# Revit family: Sanitary_Showers_hansgrohe_15854XXX-RainPad-Finish-set-for-2-functi_222
name_source: partatom
category: Plumbing Fixtures
revit_build: Autodesk Revit 2015 (Build: 20140903_1530(x64)
units: mm (PartAtom-declared; Revit-internal decimal feet)

## types (1)
- black/chrome
    Always visible = Yes
    BIMobject category = Showers
    BIMobject category code = sanitary-showers
    BIMobject main category = Sanitary
    BIMobject main category code = sanitary
    Brand url = http://www.hansgrohe-int.com
    Design country = Germany
    Edition number = 1
    GTIN code = https://4011097801841
    IFC Classification = Sanitary Terminal
    Installation instructions = https://www.hansgrohe.de
    Manufacturer country = Germany
    Manufacturer name = hansgrohe
    Material 1 = Hansgrohe - RainPad - 000 Chrome
    Material 2 = Hansgrohe - RainPad - Graphite
    Material 3 = Hansgrohe - RainPad - Black
    Material 4 = Hansgrohe - RainPad - White
    Material 5 = Hansgrohe - RainPad - FS conc.2 funct
    Product Guid = cb718294-c071-4269-aa9d-af941b143dae
    Product SKU = 15854XXX
    Product data url = https://bimobject.com
    Product name = 15854XXX RainPad Finish set for 2 functions
    Product url = https://www.hansgrohe.de
    QR code = http://bimobject.com
    Technical description = https://www.hansgrohe.de

## geometry (parser evidence)
native form markers: Sweep x3
no freeform markers — native parametric forms only
